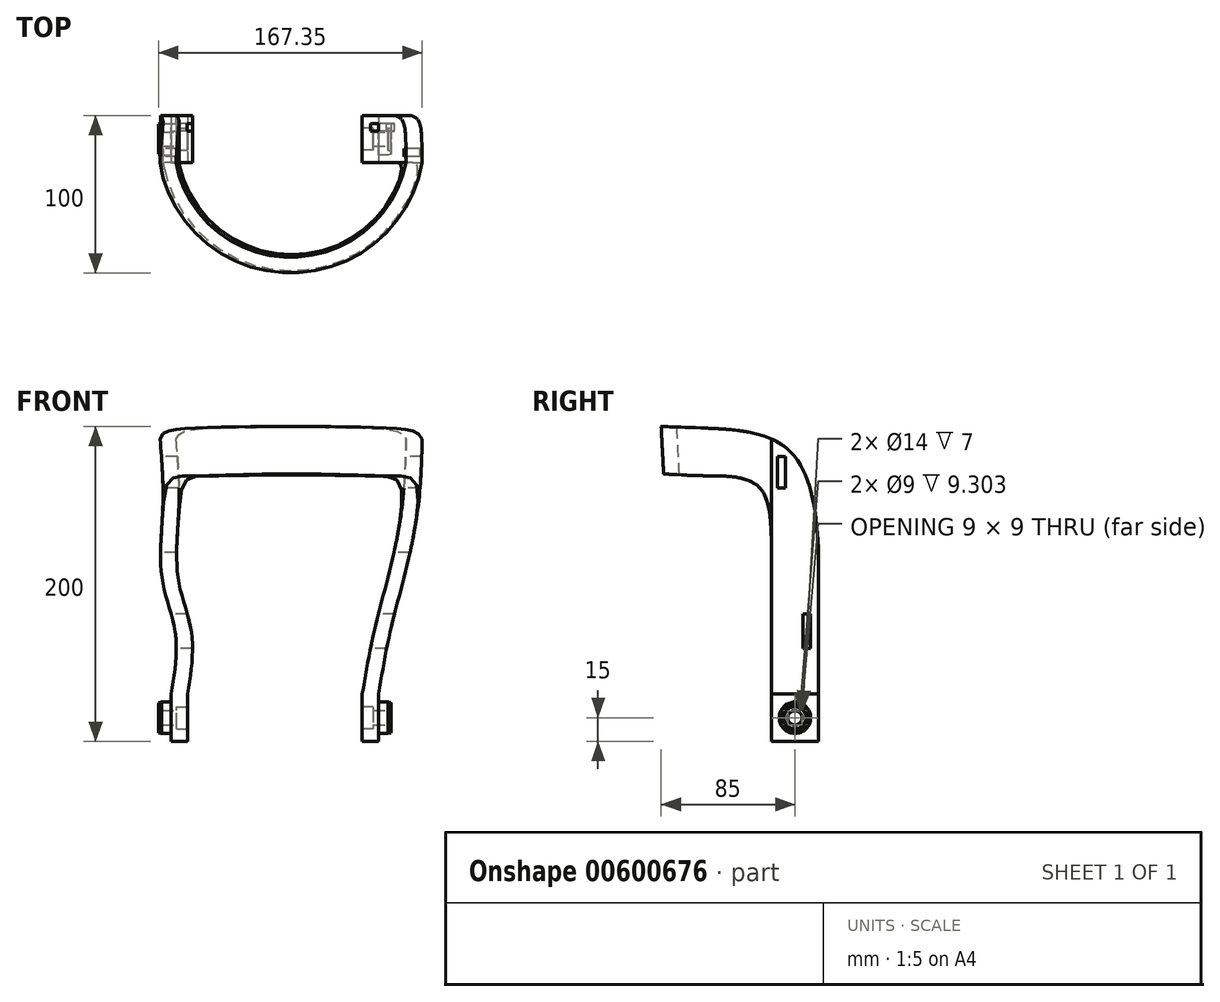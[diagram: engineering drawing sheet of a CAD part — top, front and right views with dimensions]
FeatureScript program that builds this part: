
annotation { "Feature Type Name" : "Feature", "Feature Type Description" : "" }
export const myFeature = defineFeature(function(context is Context, id is Id, definition is map)
    precondition{}
    {
        {
            var Q0;
            Q0=qCreatedBy(makeId("Top.planeOp"),FACE);
            var sketch = newSketch(context, id + "F0", { "sketchPlane" : qUnion([Q0])});
            skLineSegment(sketch, "E0", {"start": v(-55.5, 15) * mm, "end": v(-55.5, -15) * mm});
            skLineSegment(sketch, "E1", {"start": v(55.5, 15) * mm, "end": v(55.5, -15) * mm});
            skPoint(sketch, "E2", {"position": v(-55.5, 0) * mm});
            skPoint(sketch, "E3", {"position": v(55.5, 0) * mm});
            skLineSegment(sketch, "E4", {"start": v(-55.5, 15) * mm, "end": v(-65.81, 15) * mm});
            skLineSegment(sketch, "E5", {"start": v(-65.81, 15) * mm, "end": v(-65.81, -15) * mm});
            skLineSegment(sketch, "E6", {"start": v(55.5, 15) * mm, "end": v(65.81, 15) * mm});
            skLineSegment(sketch, "E7", {"start": v(65.81, 15) * mm, "end": v(65.81, -15) * mm});
            skLineSegment(sketch, "E8", {"start": v(-65.81, -15) * mm, "end": v(-55.5, -15) * mm});
            skLineSegment(sketch, "E9", {"start": v(55.5, -15) * mm, "end": v(65.81, -15) * mm});
            skSolve(sketch);
        }
        {
            var Q0;
            Q0=qCreatedBy(makeId("Top.planeOp"),FACE);
            cPlane(context, id + "F1", {"entities" : qUnion([Q0]), "cplaneType" : CPlaneType.OFFSET, "offset" : 30 * mm, "width" : 150 * mm, "height" : 150 * mm});
        }
        {
            var Q0;
            Q0=qCreatedBy(id+"F1.planeOp",FACE);
            var sketch = newSketch(context, id + "F2", { "sketchPlane" : qUnion([Q0])});
            skArc(sketch, "E10", {"start": v(-55.5, -15) * mm, "mid": v(0, -57.5) * mm, "end": v(55.5, -15) * mm});
            skArc(sketch, "E11", {"start": v(-65.81, -15) * mm, "mid": v(0, -67.5) * mm, "end": v(65.81, -15) * mm});
            skLineSegment(sketch, "E12", {"start": v(-55.5, 15) * mm, "end": v(-55.5, -15) * mm});
            skLineSegment(sketch, "E13", {"start": v(55.5, 15) * mm, "end": v(55.5, -15) * mm});
            skPoint(sketch, "E14", {"position": v(-55.5, 0) * mm});
            skPoint(sketch, "E15", {"position": v(55.5, 0) * mm});
            skLineSegment(sketch, "E16", {"start": v(-55.5, 15) * mm, "end": v(-65.81, 15) * mm});
            skLineSegment(sketch, "E17", {"start": v(-65.81, 15) * mm, "end": v(-65.81, -15) * mm});
            skLineSegment(sketch, "E18", {"start": v(55.5, 15) * mm, "end": v(65.81, 15) * mm});
            skLineSegment(sketch, "E19", {"start": v(65.81, 15) * mm, "end": v(65.81, -15) * mm});
            skSolve(sketch);
        }
        {
            var Q0;
            Q0=qCreatedBy(makeId("Top.planeOp"),FACE);
            cPlane(context, id + "F3", {"entities" : qUnion([Q0]), "cplaneType" : CPlaneType.OFFSET, "offset" : 70 * mm, "width" : 150 * mm, "height" : 150 * mm});
        }
        {
            var Q0;
            Q0=qCreatedBy(id+"F3.planeOp",FACE);
            var sketch = newSketch(context, id + "F4", { "sketchPlane" : qUnion([Q0])});
            skPoint(sketch, "E20", {"position": v(5, 0) * mm});
            skPoint(sketch, "E21.center.orphan", {"position": v(0, 0) * mm});
            skArc(sketch, "E22", {"start": v(-53.1, -15) * mm, "mid": v(5, -60) * mm, "end": v(63.1, -15) * mm});
            skArc(sketch, "E23", {"start": v(-63.37, -15) * mm, "mid": v(5, -70) * mm, "end": v(73.37, -15) * mm});
            skLineSegment(sketch, "E24", {"start": v(-53.1, 15) * mm, "end": v(-53.1, -15) * mm});
            skLineSegment(sketch, "E25", {"start": v(63.1, 15) * mm, "end": v(63.1, -15) * mm});
            skPoint(sketch, "E26", {"position": v(-53.1, 0) * mm});
            skLineSegment(sketch, "E27", {"start": v(-53.1, 15) * mm, "end": v(-63.37, 15) * mm});
            skLineSegment(sketch, "E28", {"start": v(-63.37, 15) * mm, "end": v(-63.37, -15) * mm});
            skLineSegment(sketch, "E29", {"start": v(63.1, 15) * mm, "end": v(73.37, 15) * mm});
            skLineSegment(sketch, "E30", {"start": v(73.37, 15) * mm, "end": v(73.37, -15) * mm});
            skSolve(sketch);
        }
        {
            var Q0;
            Q0=qCreatedBy(makeId("Top.planeOp"),FACE);
            cPlane(context, id + "F5", {"entities" : qUnion([Q0]), "cplaneType" : CPlaneType.OFFSET, "offset" : 100 * mm, "width" : 150 * mm, "height" : 150 * mm});
        }
        {
            var Q0;
            Q0=qCreatedBy(id+"F5.planeOp",FACE);
            var sketch = newSketch(context, id + "F6", { "sketchPlane" : qUnion([Q0])});
            skPoint(sketch, "E31", {"position": v(5, 0) * mm});
            skArc(sketch, "E32", {"start": v(-60.81, -15) * mm, "mid": v(5, -67.5) * mm, "end": v(70.81, -15) * mm});
            skArc(sketch, "E33", {"start": v(-71.03, -15) * mm, "mid": v(5, -77.5) * mm, "end": v(81.03, -15) * mm});
            skLineSegment(sketch, "E34", {"start": v(-60.81, 15) * mm, "end": v(-60.81, -15) * mm});
            skLineSegment(sketch, "E35", {"start": v(70.81, 15) * mm, "end": v(70.81, -15) * mm});
            skLineSegment(sketch, "E36", {"start": v(-60.81, 15) * mm, "end": v(-71.03, 15) * mm});
            skLineSegment(sketch, "E37", {"start": v(-71.03, 15) * mm, "end": v(-71.03, -15) * mm});
            skLineSegment(sketch, "E38", {"start": v(70.81, 15) * mm, "end": v(81.03, 15) * mm});
            skLineSegment(sketch, "E39", {"start": v(81.03, 15) * mm, "end": v(81.03, -15) * mm});
            skSolve(sketch);
        }
        {
            var Q0;
            Q0=qCreatedBy(makeId("Top.planeOp"),FACE);
            cPlane(context, id + "F7", {"entities" : qUnion([Q0]), "cplaneType" : CPlaneType.OFFSET, "offset" : 150 * mm, "width" : 150 * mm, "height" : 150 * mm});
        }
        {
            var Q0;
            Q0=qCreatedBy(id+"F7.planeOp",FACE);
            var sketch = newSketch(context, id + "F8", { "sketchPlane" : qUnion([Q0])});
            skPoint(sketch, "E40", {"position": v(10, 0) * mm});
            skArc(sketch, "E41", {"start": v(-60.93, -15) * mm, "mid": v(10, -72.5) * mm, "end": v(80.93, -15) * mm});
            skArc(sketch, "E42", {"start": v(-71.12, -15) * mm, "mid": v(10, -82.5) * mm, "end": v(91.12, -15) * mm});
            skLineSegment(sketch, "E43", {"start": v(-60.93, 15) * mm, "end": v(-60.93, -15) * mm});
            skLineSegment(sketch, "E44", {"start": v(80.93, -15) * mm, "end": v(80.93, 15) * mm});
            skPoint(sketch, "E45", {"position": v(-60.93, 0) * mm});
            skPoint(sketch, "E46", {"position": v(80.93, 0) * mm});
            skLineSegment(sketch, "E47", {"start": v(-60.93, 15) * mm, "end": v(-71.12, 15) * mm});
            skLineSegment(sketch, "E48", {"start": v(-71.12, 15) * mm, "end": v(-71.12, -15) * mm});
            skLineSegment(sketch, "E49", {"start": v(80.93, 15) * mm, "end": v(91.12, 15) * mm});
            skLineSegment(sketch, "E50", {"start": v(91.12, 15) * mm, "end": v(91.12, -15) * mm});
            skSolve(sketch);
        }
        {
            var Q0;
            Q0=qCreatedBy(makeId("Top.planeOp"),FACE);
            cPlane(context, id + "F9", {"entities" : qUnion([Q0]), "cplaneType" : CPlaneType.OFFSET, "offset" : 200 * mm, "width" : 150 * mm, "height" : 150 * mm});
        }
        {
            var Q0;
            Q0=qCreatedBy(id+"F9.planeOp",FACE);
            var sketch = newSketch(context, id + "F10", { "sketchPlane" : qUnion([Q0])});
            skPoint(sketch, "E51", {"position": v(10, 0) * mm});
            skArc(sketch, "E52", {"start": v(-63.48, -15) * mm, "mid": v(10, -75) * mm, "end": v(83.48, -15) * mm});
            skArc(sketch, "E53", {"start": v(-73.67, -15) * mm, "mid": v(10, -85) * mm, "end": v(93.67, -15) * mm});
            skLineSegment(sketch, "E54", {"start": v(-63.48, 15) * mm, "end": v(-63.48, -15) * mm});
            skLineSegment(sketch, "E55", {"start": v(83.48, 15) * mm, "end": v(83.48, -15) * mm});
            skLineSegment(sketch, "E56", {"start": v(-63.48, 15) * mm, "end": v(-73.67, 15) * mm});
            skLineSegment(sketch, "E57", {"start": v(-73.67, 15) * mm, "end": v(-73.67, -15) * mm});
            skLineSegment(sketch, "E58", {"start": v(83.48, 15) * mm, "end": v(93.67, 15) * mm});
            skLineSegment(sketch, "E59", {"start": v(93.67, 15) * mm, "end": v(93.67, -15) * mm});
            skSolve(sketch);
        }
        {
            var Q0;
            Q0 = qSketchRegion(id + "F2", true);
            var Q1;
            Q1 = qSketchRegion(id + "F4", true);
            var Q2;
            Q2 = qSketchRegion(id + "F6", true);
            var Q3;
            Q3 = qSketchRegion(id + "F8", true);
            var Q4;
            Q4 = qSketchRegion(id + "F10", true);
            loft(context, id + "F11", {"sheetProfilesArray" : [{ "sheetProfileEntities" : qUnion([Q0]) }, { "sheetProfileEntities" : qUnion([Q1]) }, { "sheetProfileEntities" : qUnion([Q2]) }, { "sheetProfileEntities" : qUnion([Q3]) }, { "sheetProfileEntities" : qUnion([Q4]) }]});
        }
        {
            var Q0;
            Q0=qCreatedBy(makeId("Right.planeOp"),FACE);
            cPlane(context, id + "F12", {"entities" : qUnion([Q0]), "cplaneType" : CPlaneType.OFFSET, "offset" : 77 * mm, "oppositeDirection" : true, "width" : 150 * mm, "height" : 150 * mm});
        }
        {
            var Q0;
            Q0=qCreatedBy(id+"F12.planeOp",FACE);
            var sketch = newSketch(context, id + "F13", { "sketchPlane" : qUnion([Q0])});
            skPoint(sketch, "E60", {"position": v(-85, 200) * mm});
            skLineSegment(sketch, "E61", {"start": v(-85, 200) * mm, "end": v(-85, 170) * mm});
            skPoint(sketch, "E62", {"position": v(15, 200) * mm});
            skLineSegment(sketch, "E63", {"start": v(15, 200) * mm, "end": v(15, 120) * mm});
            skPoint(sketch, "E64", {"position": v(15, 0) * mm});
            skPoint(sketch, "E65", {"position": v(-15, 0) * mm});
            skPoint(sketch, "E66", {"position": v(-15, 200) * mm});
            skFitSpline(sketch, "E67", {"points": [v(-85, 200) * mm, v(15, 120) * mm], "startDerivative": vector(199.24, -8.69) * mm, "endDerivative": vector(9.95, -251.27) * mm});
            skPoint(sketch, "E68", {"position": v(-56.51, 168.7) * mm});
            skPoint(sketch, "E69", {"position": v(-23.21, 161.98) * mm});
            skPoint(sketch, "E70", {"position": v(-50.86, 198.7) * mm});
            skPoint(sketch, "E71", {"position": v(-4.39, 185.34) * mm});
            skPoint(sketch, "E72", {"position": v(-15, 120) * mm});
            skFitSpline(sketch, "E73", {"points": [v(-15, 120) * mm, v(-23.21, 161.98) * mm, v(-56.51, 168.7) * mm, v(-85, 170) * mm], "startDerivative": vector(0.5, 138.75) * mm, "endDerivative": vector(-88.02, 5.85) * mm});
            skLineSegment(sketch, "E74", {"start": v(-15, 120) * mm, "end": v(-15, 0) * mm});
            skLineSegment(sketch, "E75", {"start": v(15, 0) * mm, "end": v(15, 120) * mm});
            skLineSegment(sketch, "E76", {"start": v(-85, 200) * mm, "end": v(15, 200) * mm});
            skLineSegment(sketch, "E77", {"start": v(-85, 170) * mm, "end": v(-82.46, 0) * mm});
            skLineSegment(sketch, "E78", {"start": v(-82.46, 0) * mm, "end": v(-15, 0) * mm});
            skLineSegment(sketch, "E79", {"start": v(-85, 170) * mm, "end": v(-85, 200) * mm});
            skSolve(sketch);
        }
        {
            var Q0;
            Q0 = qSketchRegion(id + "F13", true);
            extrude(context, id + "F14", {"entities" : qUnion([Q0]), "operationType" : NewBodyOperationType.REMOVE, "depth" : 300 * mm, "offsetDistance" : 25 * mm});
        }
        {
            var Q0;
            Q0=qCreatedBy(id+"F12.planeOp",FACE);
            var sketch = newSketch(context, id + "F15", { "sketchPlane" : qUnion([Q0])});
            skPoint(sketch, "E80", {"position": v(7.5, 70) * mm});
            skLineSegment(sketch, "E81.bottom", {"start": v(10, 81) * mm, "end": v(5, 81) * mm});
            skLineSegment(sketch, "E81.top", {"start": v(10, 59) * mm, "end": v(5, 59) * mm});
            skLineSegment(sketch, "E81.left", {"start": v(10, 81) * mm, "end": v(10, 59) * mm});
            skLineSegment(sketch, "E81.right", {"start": v(5, 81) * mm, "end": v(5, 59) * mm});
            skPoint(sketch, "E82", {"position": v(15, 0) * mm});
            skLineSegment(sketch, "E83", {"start": v(15, 0) * mm, "end": v(15, 89.37) * mm});
            skPoint(sketch, "E84", {"position": v(15, 70) * mm});
            skSolve(sketch);
        }
        {
            var Q0;
            Q0 = qSketchRegion(id + "F15", true);
            extrude(context, id + "F16", {"entities" : qUnion([Q0]), "operationType" : NewBodyOperationType.REMOVE, "depth" : 192.9 * mm, "offsetDistance" : 25 * mm});
        }
        {
            var Q0;
            Q0=qCreatedBy(id+"F12.planeOp",FACE);
            var sketch = newSketch(context, id + "F17", { "sketchPlane" : qUnion([Q0])});
            skPoint(sketch, "E85", {"position": v(-8.62, 171.05) * mm});
            skLineSegment(sketch, "E86.bottom", {"start": v(-11.12, 161.05) * mm, "end": v(-6.12, 161.05) * mm});
            skLineSegment(sketch, "E86.top", {"start": v(-11.12, 181.05) * mm, "end": v(-6.12, 181.05) * mm});
            skLineSegment(sketch, "E86.left", {"start": v(-11.12, 161.05) * mm, "end": v(-11.12, 181.05) * mm});
            skLineSegment(sketch, "E86.right", {"start": v(-6.12, 161.05) * mm, "end": v(-6.12, 181.05) * mm});
            skSolve(sketch);
        }
        {
            var Q0;
            Q0 = qSketchRegion(id + "F17", true);
            extrude(context, id + "F18", {"entities" : qUnion([Q0]), "operationType" : NewBodyOperationType.REMOVE, "depth" : 239 * mm, "offsetDistance" : 25 * mm});
        }
        {
            var Q0;
            Q0 = qSketchRegion(id + "F0", true);
            extrude(context, id + "F19", {"entities" : qUnion([Q0]), "operationType" : NewBodyOperationType.ADD, "depth" : 30 * mm, "offsetDistance" : 25 * mm});
        }
        {
            var Q0;
            Q0=makeQuery(id+"F19.opExtrude","SWEPT_FACE",FACE,{"disambiguationData":[OSD([sQuery(id+"F0.wireOp",EDGE,"E7")])]});
            var sketch = newSketch(context, id + "F20", { "sketchPlane" : qUnion([Q0])});
            skPoint(sketch, "E87", {"position": v(-15, 30) * mm});
            skPoint(sketch, "E88", {"position": v(-15, 0) * mm});
            skPoint(sketch, "E89", {"position": v(0, 15) * mm});
            skCircle(sketch, "E90", {"center": v(0, 15) * mm, "radius": 10 * mm});
            skSolve(sketch);
        }
        {
            var Q0;
            Q0 = qSketchRegion(id + "F20", true);
            extrude(context, id + "F21", {"entities" : qUnion([Q0]), "operationType" : NewBodyOperationType.ADD, "depth" : 6 * mm, "offsetDistance" : 25 * mm});
        }
        {
            var Q0;
            Q0=makeQuery(id+"F21.opExtrude","CAP_FACE",FACE,{"disambiguationData":[OSD([sQuery(id+"F20.wireOp",EDGE,"E90")])],"isStart":false});
            cPlane(context, id + "F22", {"entities" : qUnion([Q0]), "cplaneType" : CPlaneType.OFFSET, "offset" : 0 * mm, "width" : 150 * mm, "height" : 150 * mm});
        }
        {
            var Q0;
            Q0=makeQuery(id+"F19.opExtrude","SWEPT_FACE",FACE,{"disambiguationData":[OSD([sQuery(id+"F0.wireOp",EDGE,"E1")])]});
            cPlane(context, id + "F23", {"entities" : qUnion([Q0]), "cplaneType" : CPlaneType.OFFSET, "offset" : 0 * mm, "width" : 150 * mm, "height" : 150 * mm});
        }
        {
            var Q0;
            Q0=qCreatedBy(id+"F23.planeOp",FACE);
            var sketch = newSketch(context, id + "F24", { "sketchPlane" : qUnion([Q0])});
            skPoint(sketch, "E91", {"position": v(0, 0) * mm});
            skPoint(sketch, "E92", {"position": v(0, 15) * mm});
            skCircle(sketch, "E93", {"center": v(0, 15) * mm, "radius": 7 * mm});
            skSolve(sketch);
        }
        {
            var Q0;
            Q0 = qSketchRegion(id + "F24", true);
            extrude(context, id + "F25", {"entities" : qUnion([Q0]), "operationType" : NewBodyOperationType.REMOVE, "oppositeDirection" : true, "depth" : 7 * mm, "offsetDistance" : 25 * mm});
        }
        {
            var Q0;
            Q0=makeQuery(id+"F19.opExtrude","SWEPT_FACE",FACE,{"disambiguationData":[OSD([sQuery(id+"F0.wireOp",EDGE,"E5")])]});
            cPlane(context, id + "F26", {"entities" : qUnion([Q0]), "cplaneType" : CPlaneType.OFFSET, "offset" : 0 * mm, "width" : 150 * mm, "height" : 150 * mm});
        }
        {
            var Q0;
            Q0=qCreatedBy(id+"F26.planeOp",FACE);
            var sketch = newSketch(context, id + "F27", { "sketchPlane" : qUnion([Q0])});
            skPoint(sketch, "E94", {"position": v(0, 15) * mm});
            skCircle(sketch, "E95", {"center": v(0, 15) * mm, "radius": 10 * mm});
            skSolve(sketch);
        }
        {
            var Q0;
            Q0 = qSketchRegion(id + "F27", true);
            extrude(context, id + "F28", {"entities" : qUnion([Q0]), "operationType" : NewBodyOperationType.ADD, "depth" : 6 * mm, "offsetDistance" : 25 * mm});
        }
        {
            var Q0;
            Q0=makeQuery(id+"F28.opExtrude","CAP_FACE",FACE,{"disambiguationData":[OSD([sQuery(id+"F27.wireOp",EDGE,"E95")])],"isStart":false});
            cPlane(context, id + "F29", {"entities" : qUnion([Q0]), "cplaneType" : CPlaneType.OFFSET, "offset" : 0 * mm, "width" : 150 * mm, "height" : 150 * mm});
        }
        {
            var Q0;
            Q0=makeQuery(id+"F19.opExtrude","SWEPT_FACE",FACE,{"disambiguationData":[OSD([sQuery(id+"F0.wireOp",EDGE,"E0")])]});
            cPlane(context, id + "F30", {"entities" : qUnion([Q0]), "cplaneType" : CPlaneType.OFFSET, "offset" : 0 * mm, "width" : 150 * mm, "height" : 150 * mm});
        }
        {
            var Q0;
            Q0=qCreatedBy(id+"F30.planeOp",FACE);
            var sketch = newSketch(context, id + "F31", { "sketchPlane" : qUnion([Q0])});
            skPoint(sketch, "E96", {"position": v(0, 0) * mm});
            skPoint(sketch, "E97", {"position": v(0, 15) * mm});
            skCircle(sketch, "E98", {"center": v(0, 15) * mm, "radius": 7 * mm});
            skSolve(sketch);
        }
        {
            var Q0;
            Q0 = qSketchRegion(id + "F31", true);
            extrude(context, id + "F32", {"entities" : qUnion([Q0]), "operationType" : NewBodyOperationType.REMOVE, "oppositeDirection" : true, "depth" : 7 * mm, "offsetDistance" : 25 * mm});
        }
        {
            var Q0;
            Q0=makeQuery(id+"F19.opExtrude","CAP_FACE",FACE,{"disambiguationData":[OSD([sQuery(id+"F0.wireOp",EDGE,"E1"),sQuery(id+"F0.wireOp",EDGE,"E6"),sQuery(id+"F0.wireOp",EDGE,"E7"),sQuery(id+"F0.wireOp",EDGE,"E9")])],"isStart":true});
            cPlane(context, id + "F33", {"entities" : qUnion([Q0]), "cplaneType" : CPlaneType.OFFSET, "offset" : 15 * mm, "oppositeDirection" : true, "width" : 150 * mm, "height" : 150 * mm});
        }
        {
            var Q0;
            Q0=qCreatedBy(id+"F33.planeOp",FACE);
            var sketch = newSketch(context, id + "F34", { "sketchPlane" : qUnion([Q0])});
            skPoint(sketch, "E99", {"position": v(60.66, -15) * mm});
            skLineSegment(sketch, "E100", {"start": v(60.66, -15) * mm, "end": v(61.72, -15) * mm, "construction": true});
            skPoint(sketch, "E101", {"position": v(71.81, 4.05) * mm});
            skPoint(sketch, "E102", {"position": v(71.81, -12) * mm});
            skPoint(sketch, "E103", {"position": v(71.81, -15) * mm});
            skPoint(sketch, "E104", {"position": v(41.37, 7.31) * mm});
            skPoint(sketch, "E105", {"position": v(71.81, -13.5) * mm});
            skPoint(sketch, "E106", {"position": v(73.81, -13.5) * mm});
            skPoint(sketch, "E107", {"position": v(73.81, -12.5) * mm});
            skPoint(sketch, "E108", {"position": v(73.81, -14.5) * mm});
            skLineSegment(sketch, "E109", {"start": v(71.81, -12) * mm, "end": v(71.81, -15) * mm});
            skPoint(sketch, "E110", {"position": v(71.81, 0) * mm});
            skPoint(sketch, "E111", {"position": v(71.81, -10) * mm});
            skPoint(sketch, "E112", {"position": v(65.81, -10) * mm});
            skPoint(sketch, "E113", {"position": v(65.81, -7) * mm});
            skPoint(sketch, "E114", {"position": v(65.81, -8.5) * mm});
            skPoint(sketch, "E115", {"position": v(67.81, -8.5) * mm});
            skPoint(sketch, "E116", {"position": v(67.81, -7.5) * mm});
            skPoint(sketch, "E117", {"position": v(67.81, -9.5) * mm});
            skPoint(sketch, "E118", {"position": v(65.81, 0) * mm});
            skLineSegment(sketch, "E119.trimOffspring", {"start": v(71.81, -10) * mm, "end": v(71.81, -16.41) * mm, "construction": true});
            skPoint(sketch, "E120", {"position": v(71.81, -7) * mm});
            skPoint(sketch, "E121", {"position": v(71.81, -8.5) * mm});
            skPoint(sketch, "E122", {"position": v(73.81, -8.5) * mm});
            skPoint(sketch, "E123", {"position": v(73.81, -7.5) * mm});
            skPoint(sketch, "E124", {"position": v(73.81, -9.5) * mm});
            skLineSegment(sketch, "E125", {"start": v(73.81, -7.5) * mm, "end": v(71.81, -7) * mm});
            skLineSegment(sketch, "E126", {"start": v(73.81, -9.5) * mm, "end": v(73.81, -7.5) * mm});
            skLineSegment(sketch, "E127", {"start": v(73.81, -9.5) * mm, "end": v(71.81, -10) * mm});
            skLineSegment(sketch, "E128", {"start": v(71.81, -7) * mm, "end": v(71.81, -10) * mm});
            skLineSegment(sketch, "E129", {"start": v(71.81, 0) * mm, "end": v(73.81, 0) * mm});
            skLineSegment(sketch, "E130", {"start": v(73.81, -8.5) * mm, "end": v(73.81, -9.5) * mm});
            skSolve(sketch);
        }
        {
            var Q0;
            Q0 = qSketchRegion(id + "F34", true);
            var Q1;
            Q1=sQuery(id+"F34.wireOp",EDGE,"E129");
            revolve(context, id + "F35", {"operationType" : NewBodyOperationType.ADD, "entities" : qUnion([Q0]), "axis" : qUnion([Q1]), "revolveType" : RevolveType.FULL});
        }
        {
            var Q0;
            Q0=qCreatedBy(id+"F22.planeOp",FACE);
            var sketch = newSketch(context, id + "F36", { "sketchPlane" : qUnion([Q0])});
            skPoint(sketch, "E131", {"position": v(0, 15) * mm});
            skPoint(sketch, "E132", {"position": v(0, 0) * mm});
            skCircle(sketch, "E133", {"center": v(0, 15) * mm, "radius": 4.5 * mm});
            skSolve(sketch);
        }
        {
            var Q0;
            Q0 = qSketchRegion(id + "F36", true);
            extrude(context, id + "F37", {"entities" : qUnion([Q0]), "operationType" : NewBodyOperationType.REMOVE, "oppositeDirection" : true, "depth" : 25 * mm, "offsetDistance" : 25 * mm});
        }
        {
            var Q0;
            Q0=makeQuery(id+"F19.opExtrude","CAP_FACE",FACE,{"disambiguationData":[OSD([sQuery(id+"F0.wireOp",EDGE,"E0"),sQuery(id+"F0.wireOp",EDGE,"E4"),sQuery(id+"F0.wireOp",EDGE,"E5"),sQuery(id+"F0.wireOp",EDGE,"E8")])],"isStart":true});
            cPlane(context, id + "F38", {"entities" : qUnion([Q0]), "cplaneType" : CPlaneType.OFFSET, "offset" : 15 * mm, "oppositeDirection" : true, "width" : 150 * mm, "height" : 150 * mm});
        }
        {
            var Q0;
            Q0=qCreatedBy(id+"F38.planeOp",FACE);
            var sketch = newSketch(context, id + "F39", { "sketchPlane" : qUnion([Q0])});
            skPoint(sketch, "E134", {"position": v(-60.91, -32.93) * mm});
            skPoint(sketch, "E135", {"position": v(-65.81, -10) * mm});
            skPoint(sketch, "E136", {"position": v(-57.6, -34.18) * mm});
            skPoint(sketch, "E137", {"position": v(-65.81, -15) * mm});
            skPoint(sketch, "E138", {"position": v(-71.81, -10) * mm});
            skPoint(sketch, "E139", {"position": v(-71.81, -7) * mm});
            skPoint(sketch, "E140", {"position": v(-71.81, -8.5) * mm});
            skPoint(sketch, "E141", {"position": v(-73.81, -8.5) * mm});
            skPoint(sketch, "E142", {"position": v(-73.81, -9.5) * mm});
            skPoint(sketch, "E143", {"position": v(-73.81, -7.5) * mm});
            skLineSegment(sketch, "E144", {"start": v(-73.81, -9.5) * mm, "end": v(-71.81, -10) * mm});
            skLineSegment(sketch, "E145", {"start": v(-73.81, -7.5) * mm, "end": v(-73.81, -9.5) * mm});
            skLineSegment(sketch, "E146", {"start": v(-73.81, -7.5) * mm, "end": v(-71.81, -7) * mm});
            skLineSegment(sketch, "E147", {"start": v(-71.81, -10) * mm, "end": v(-71.81, -7) * mm});
            skLineSegment(sketch, "E148", {"start": v(-73.81, -8.5) * mm, "end": v(-73.81, -7.5) * mm});
            skSolve(sketch);
        }
        {
            var Q0;
            Q0=qCreatedBy(id+"F38.planeOp",FACE);
            var sketch = newSketch(context, id + "F40", { "sketchPlane" : qUnion([Q0])});
            skPoint(sketch, "E149", {"position": v(-71.81, -10) * mm});
            skPoint(sketch, "E150", {"position": v(-71.81, 0) * mm});
            skLineSegment(sketch, "E151", {"start": v(-71.81, 0) * mm, "end": v(-73.81, 0) * mm});
            skSolve(sketch);
        }
        {
            var Q0;
            Q0 = qSketchRegion(id + "F39", true);
            var Q1;
            Q1=sQuery(id+"F40.wireOp",EDGE,"E151");
            revolve(context, id + "F41", {"operationType" : NewBodyOperationType.ADD, "entities" : qUnion([Q0]), "axis" : qUnion([Q1]), "revolveType" : RevolveType.FULL});
        }
        {
            var Q0;
            Q0=qCreatedBy(id+"F30.planeOp",FACE);
            var sketch = newSketch(context, id + "F42", { "sketchPlane" : qUnion([Q0])});
            skPoint(sketch, "E152", {"position": v(0, 0) * mm});
            skPoint(sketch, "E153", {"position": v(0, 15) * mm});
            skCircle(sketch, "E154", {"center": v(0, 15) * mm, "radius": 4.5 * mm});
            skSolve(sketch);
        }
        {
            var Q0;
            Q0 = qSketchRegion(id + "F42", true);
            extrude(context, id + "F43", {"entities" : qUnion([Q0]), "operationType" : NewBodyOperationType.REMOVE, "oppositeDirection" : true, "depth" : 25 * mm, "offsetDistance" : 25 * mm});
        }
    });
